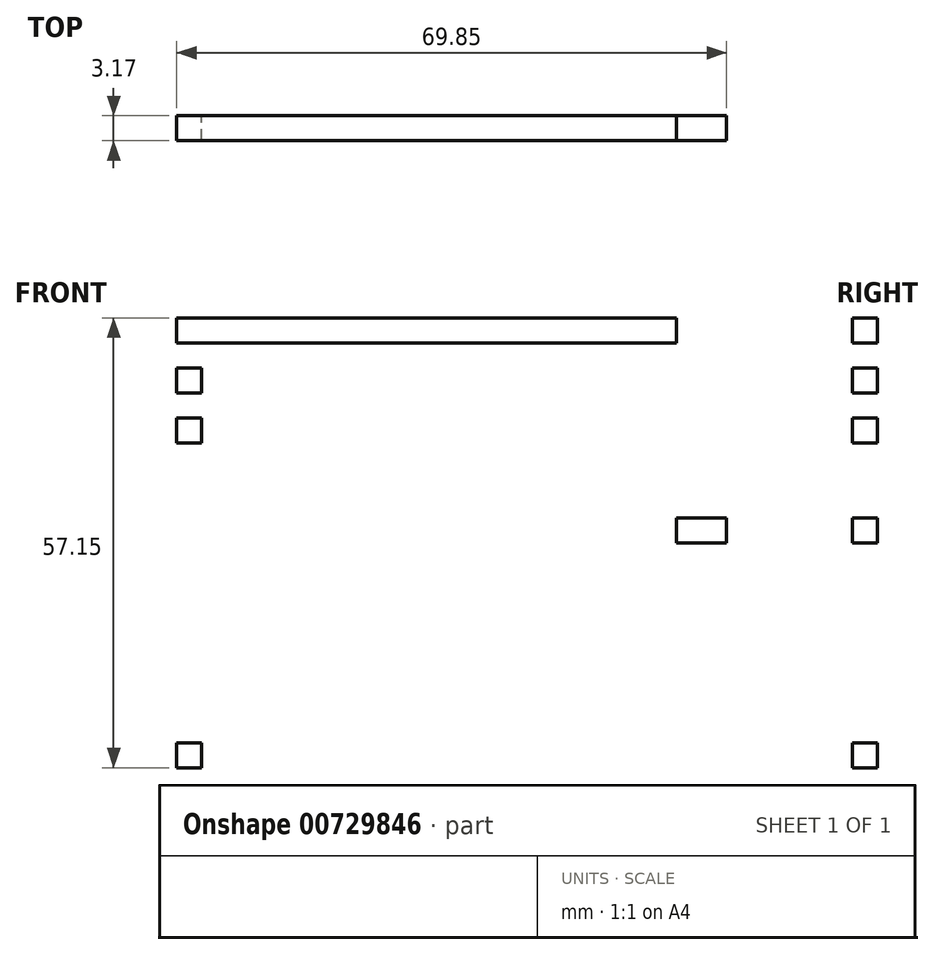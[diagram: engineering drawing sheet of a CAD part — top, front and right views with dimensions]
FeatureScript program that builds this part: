
annotation { "Feature Type Name" : "Feature", "Feature Type Description" : "" }
export const myFeature = defineFeature(function(context is Context, id is Id, definition is map)
    precondition{}
    {
        {
            var Q0;
            Q0=qCreatedBy(makeId("Front.planeOp"),FACE);
            var sketch = newSketch(context, id + "F0", { "sketchPlane" : qUnion([Q0])});
            skLineSegment(sketch, "E0.bottom", {"start": v(-59.86, 11.25) * mm, "end": v(13.17, 11.25) * mm});
            skLineSegment(sketch, "E0.top", {"start": v(-59.86, -39.55) * mm, "end": v(13.17, -39.55) * mm});
            skLineSegment(sketch, "E0.left", {"start": v(-59.86, 11.25) * mm, "end": v(-59.86, -39.55) * mm});
            skLineSegment(sketch, "E0.right", {"start": v(13.17, 11.25) * mm, "end": v(13.17, -39.55) * mm});
            skLineSegment(sketch, "E1.bottom", {"start": v(-53.5, -39.55) * mm, "end": v(10, -39.55) * mm});
            skLineSegment(sketch, "E1.top", {"start": v(-53.5, -42.73) * mm, "end": v(6.82, -42.73) * mm});
            skLineSegment(sketch, "E1.left", {"start": v(-53.5, -39.55) * mm, "end": v(-53.5, -42.73) * mm});
            skLineSegment(sketch, "E2.bottom", {"start": v(-56.68, 11.25) * mm, "end": v(6.82, 11.25) * mm});
            skLineSegment(sketch, "E2.top", {"start": v(-56.68, 14.42) * mm, "end": v(6.82, 14.42) * mm});
            skLineSegment(sketch, "E2.left", {"start": v(-56.68, 11.25) * mm, "end": v(-56.68, 14.42) * mm});
            skLineSegment(sketch, "E2.right", {"start": v(6.82, 11.25) * mm, "end": v(6.82, 14.42) * mm});
            skLineSegment(sketch, "E3.bottom", {"start": v(-56.68, 11.25) * mm, "end": v(-59.86, 11.25) * mm});
            skLineSegment(sketch, "E3.top", {"start": v(-56.68, -39.55) * mm, "end": v(-59.86, -39.55) * mm});
            skLineSegment(sketch, "E3.left", {"start": v(-56.68, 11.25) * mm, "end": v(-56.68, -39.55) * mm});
            skLineSegment(sketch, "E4.bottom", {"start": v(-53.5, -39.55) * mm, "end": v(-59.86, -39.55) * mm});
            skLineSegment(sketch, "E4.top", {"start": v(-53.5, 4.9) * mm, "end": v(-59.86, 4.9) * mm});
            skLineSegment(sketch, "E4.left", {"start": v(-53.5, -39.55) * mm, "end": v(-53.5, 4.9) * mm});
            skLineSegment(sketch, "E4.right", {"start": v(-59.86, -39.55) * mm, "end": v(-59.86, 4.9) * mm});
            skLineSegment(sketch, "E5.top", {"start": v(-56.68, -1.45) * mm, "end": v(-59.86, -1.45) * mm});
            skLineSegment(sketch, "E5.left", {"start": v(-56.68, -39.55) * mm, "end": v(-56.68, -1.45) * mm});
            skLineSegment(sketch, "E5.right", {"start": v(-59.86, -39.55) * mm, "end": v(-59.86, -1.45) * mm});
            skLineSegment(sketch, "E6.top", {"start": v(-56.68, -7.8) * mm, "end": v(-59.86, -7.8) * mm});
            skLineSegment(sketch, "E6.left", {"start": v(-56.68, -39.55) * mm, "end": v(-56.68, -7.8) * mm});
            skLineSegment(sketch, "E6.right", {"start": v(-59.86, -39.55) * mm, "end": v(-59.86, -7.8) * mm});
            skLineSegment(sketch, "E7.top", {"start": v(-53.5, -20.5) * mm, "end": v(-59.86, -20.5) * mm});
            skLineSegment(sketch, "E7.left", {"start": v(-53.5, -39.55) * mm, "end": v(-53.5, -20.5) * mm});
            skLineSegment(sketch, "E7.right", {"start": v(-59.86, -39.55) * mm, "end": v(-59.86, -20.5) * mm});
            skLineSegment(sketch, "E8.bottom", {"start": v(-59.86, -14.15) * mm, "end": v(-53.5, -14.15) * mm});
            skLineSegment(sketch, "E8.top", {"start": v(-59.86, -39.55) * mm, "end": v(-53.5, -39.55) * mm});
            skLineSegment(sketch, "E8.left", {"start": v(-59.86, -14.15) * mm, "end": v(-59.86, -39.55) * mm});
            skLineSegment(sketch, "E8.right", {"start": v(-53.5, -14.15) * mm, "end": v(-53.5, -39.55) * mm});
            skLineSegment(sketch, "E9.bottom", {"start": v(-59.86, -26.85) * mm, "end": v(-53.5, -26.85) * mm});
            skLineSegment(sketch, "E9.left", {"start": v(-59.86, -26.85) * mm, "end": v(-59.86, -39.55) * mm});
            skLineSegment(sketch, "E9.right", {"start": v(-53.5, -26.85) * mm, "end": v(-53.5, -39.55) * mm});
            skLineSegment(sketch, "E10.bottom", {"start": v(-59.86, -33.2) * mm, "end": v(-56.68, -33.2) * mm});
            skLineSegment(sketch, "E10.top", {"start": v(-59.86, -39.55) * mm, "end": v(-56.68, -39.55) * mm});
            skLineSegment(sketch, "E10.left", {"start": v(-59.86, -33.2) * mm, "end": v(-59.86, -39.55) * mm});
            skLineSegment(sketch, "E10.right", {"start": v(-56.68, -33.2) * mm, "end": v(-56.68, -39.55) * mm});
            skLineSegment(sketch, "E11.bottom", {"start": v(6.82, 11.25) * mm, "end": v(13.17, 11.25) * mm});
            skLineSegment(sketch, "E11.top", {"start": v(6.82, -33.2) * mm, "end": v(13.17, -33.2) * mm});
            skLineSegment(sketch, "E11.left", {"start": v(6.82, 11.25) * mm, "end": v(6.82, -33.2) * mm});
            skLineSegment(sketch, "E11.right", {"start": v(13.17, 11.25) * mm, "end": v(13.17, -33.2) * mm});
            skLineSegment(sketch, "E12.top", {"start": v(6.82, -26.85) * mm, "end": v(13.17, -26.85) * mm});
            skLineSegment(sketch, "E12.left", {"start": v(6.82, 11.25) * mm, "end": v(6.82, -26.85) * mm});
            skLineSegment(sketch, "E12.right", {"start": v(13.17, 11.25) * mm, "end": v(13.17, -26.85) * mm});
            skLineSegment(sketch, "E13.top", {"start": v(6.82, -39.55) * mm, "end": v(13.17, -39.55) * mm});
            skLineSegment(sketch, "E13.left", {"start": v(6.82, 11.25) * mm, "end": v(6.82, -39.55) * mm});
            skLineSegment(sketch, "E14.top", {"start": v(6.82, -14.15) * mm, "end": v(13.17, -14.15) * mm});
            skLineSegment(sketch, "E14.left", {"start": v(6.82, 11.25) * mm, "end": v(6.82, -14.15) * mm});
            skLineSegment(sketch, "E14.right", {"start": v(13.17, 11.25) * mm, "end": v(13.17, -14.15) * mm});
            skLineSegment(sketch, "E15.top", {"start": v(6.82, -20.5) * mm, "end": v(13.17, -20.5) * mm});
            skLineSegment(sketch, "E15.left", {"start": v(6.82, 11.25) * mm, "end": v(6.82, -20.5) * mm});
            skLineSegment(sketch, "E15.right", {"start": v(13.17, 11.25) * mm, "end": v(13.17, -20.5) * mm});
            skLineSegment(sketch, "E16.top", {"start": v(6.82, -7.8) * mm, "end": v(13.17, -7.8) * mm});
            skLineSegment(sketch, "E16.left", {"start": v(6.82, 11.25) * mm, "end": v(6.82, -7.8) * mm});
            skLineSegment(sketch, "E16.right", {"start": v(13.17, 11.25) * mm, "end": v(13.17, -7.8) * mm});
            skLineSegment(sketch, "E17.top", {"start": v(6.82, -1.45) * mm, "end": v(13.17, -1.45) * mm});
            skLineSegment(sketch, "E17.left", {"start": v(6.82, 11.25) * mm, "end": v(6.82, -1.45) * mm});
            skLineSegment(sketch, "E17.right", {"start": v(13.17, 11.25) * mm, "end": v(13.17, -1.45) * mm});
            skLineSegment(sketch, "E18.top", {"start": v(6.82, 4.9) * mm, "end": v(13.17, 4.9) * mm});
            skLineSegment(sketch, "E18.left", {"start": v(6.82, 11.25) * mm, "end": v(6.82, 4.9) * mm});
            skLineSegment(sketch, "E18.right", {"start": v(13.17, 11.25) * mm, "end": v(13.17, 4.9) * mm});
            skLineSegment(sketch, "E19", {"start": v(-59.86, -7.8) * mm, "end": v(-53.5, -7.8) * mm});
            skLineSegment(sketch, "E20", {"start": v(-53.5, -42.73) * mm, "end": v(-53.5, 11.25) * mm});
            skLineSegment(sketch, "E21", {"start": v(-59.86, -1.45) * mm, "end": v(-53.5, -1.45) * mm});
            skLineSegment(sketch, "E22", {"start": v(-59.86, -33.2) * mm, "end": v(-53.5, -33.2) * mm});
            skLineSegment(sketch, "E23.bottom", {"start": v(6.82, -39.55) * mm, "end": v(-53.5, -39.55) * mm});
            skLineSegment(sketch, "E23.top", {"start": v(6.82, -42.73) * mm, "end": v(-53.5, -42.73) * mm});
            skLineSegment(sketch, "E23.left", {"start": v(6.82, -39.55) * mm, "end": v(6.82, -42.73) * mm});
            skLineSegment(sketch, "E24", {"start": v(10, -39.55) * mm, "end": v(10, 11.25) * mm});
            skLineSegment(sketch, "E25.bottom", {"start": v(13.17, 11.25) * mm, "end": v(6.82, 11.25) * mm});
            skLineSegment(sketch, "E25.top", {"start": v(13.17, 8.07) * mm, "end": v(6.82, 8.07) * mm});
            skLineSegment(sketch, "E25.left", {"start": v(13.17, 11.25) * mm, "end": v(13.17, 8.07) * mm});
            skLineSegment(sketch, "E25.right", {"start": v(6.82, 11.25) * mm, "end": v(6.82, 8.07) * mm});
            skLineSegment(sketch, "E26.bottom", {"start": v(13.17, 4.9) * mm, "end": v(6.82, 4.9) * mm});
            skLineSegment(sketch, "E26.top", {"start": v(13.17, 1.72) * mm, "end": v(6.82, 1.72) * mm});
            skLineSegment(sketch, "E26.left", {"start": v(13.17, 4.9) * mm, "end": v(13.17, 1.72) * mm});
            skLineSegment(sketch, "E26.right", {"start": v(6.82, 4.9) * mm, "end": v(6.82, 1.72) * mm});
            skLineSegment(sketch, "E27.bottom", {"start": v(13.17, -1.45) * mm, "end": v(6.82, -1.45) * mm});
            skLineSegment(sketch, "E27.top", {"start": v(13.17, -4.63) * mm, "end": v(6.82, -4.63) * mm});
            skLineSegment(sketch, "E27.left", {"start": v(13.17, -1.45) * mm, "end": v(13.17, -4.63) * mm});
            skLineSegment(sketch, "E27.right", {"start": v(6.82, -1.45) * mm, "end": v(6.82, -4.63) * mm});
            skLineSegment(sketch, "E28.bottom", {"start": v(13.17, -7.8) * mm, "end": v(6.82, -7.8) * mm});
            skLineSegment(sketch, "E28.top", {"start": v(13.17, -10.98) * mm, "end": v(6.82, -10.98) * mm});
            skLineSegment(sketch, "E28.left", {"start": v(13.17, -7.8) * mm, "end": v(13.17, -10.98) * mm});
            skLineSegment(sketch, "E28.right", {"start": v(6.82, -7.8) * mm, "end": v(6.82, -10.98) * mm});
            skLineSegment(sketch, "E29.bottom", {"start": v(-59.86, 11.25) * mm, "end": v(-53.5, 11.25) * mm});
            skLineSegment(sketch, "E29.top", {"start": v(-59.86, 8.07) * mm, "end": v(-53.5, 8.07) * mm});
            skLineSegment(sketch, "E29.left", {"start": v(-59.86, 11.25) * mm, "end": v(-59.86, 8.07) * mm});
            skLineSegment(sketch, "E29.right", {"start": v(-53.5, 11.25) * mm, "end": v(-53.5, 8.07) * mm});
            skLineSegment(sketch, "E30.top", {"start": v(-53.5, 1.72) * mm, "end": v(-59.86, 1.72) * mm});
            skLineSegment(sketch, "E30.left", {"start": v(-53.5, 4.9) * mm, "end": v(-53.5, 1.72) * mm});
            skLineSegment(sketch, "E30.right", {"start": v(-59.86, 4.9) * mm, "end": v(-59.86, 1.72) * mm});
            skPoint(sketch, "E31.oppositeSnap0", {"position": v(-56.68, -36.38) * mm});
            skLineSegment(sketch, "E31.top", {"start": v(-59.86, -36.38) * mm, "end": v(-53.5, -36.38) * mm});
            skLineSegment(sketch, "E31.left", {"start": v(-59.86, -39.55) * mm, "end": v(-59.86, -36.38) * mm});
            skLineSegment(sketch, "E31.right", {"start": v(-53.5, -39.55) * mm, "end": v(-53.5, -36.38) * mm});
            skLineSegment(sketch, "E32.top", {"start": v(-59.86, -30.03) * mm, "end": v(-53.5, -30.03) * mm});
            skLineSegment(sketch, "E32.left", {"start": v(-59.86, -33.2) * mm, "end": v(-59.86, -30.03) * mm});
            skLineSegment(sketch, "E32.right", {"start": v(-53.5, -33.2) * mm, "end": v(-53.5, -30.03) * mm});
            skLineSegment(sketch, "E33.top", {"start": v(-59.86, -23.68) * mm, "end": v(-53.5, -23.68) * mm});
            skLineSegment(sketch, "E33.left", {"start": v(-59.86, -26.85) * mm, "end": v(-59.86, -23.68) * mm});
            skLineSegment(sketch, "E33.right", {"start": v(-53.5, -26.85) * mm, "end": v(-53.5, -23.68) * mm});
            skLineSegment(sketch, "E34.bottom", {"start": v(-59.86, -20.5) * mm, "end": v(-53.5, -20.5) * mm});
            skLineSegment(sketch, "E34.top", {"start": v(-59.86, -17.33) * mm, "end": v(-53.5, -17.33) * mm});
            skLineSegment(sketch, "E34.left", {"start": v(-59.86, -20.5) * mm, "end": v(-59.86, -17.33) * mm});
            skLineSegment(sketch, "E34.right", {"start": v(-53.5, -20.5) * mm, "end": v(-53.5, -17.33) * mm});
            skLineSegment(sketch, "E35.top", {"start": v(-59.86, -10.98) * mm, "end": v(-53.5, -10.98) * mm});
            skLineSegment(sketch, "E35.left", {"start": v(-59.86, -14.15) * mm, "end": v(-59.86, -10.98) * mm});
            skLineSegment(sketch, "E35.right", {"start": v(-53.5, -14.15) * mm, "end": v(-53.5, -10.98) * mm});
            skLineSegment(sketch, "E36.bottom", {"start": v(-53.5, -7.8) * mm, "end": v(-59.86, -7.8) * mm});
            skLineSegment(sketch, "E36.top", {"start": v(-53.5, -4.63) * mm, "end": v(-59.86, -4.63) * mm});
            skLineSegment(sketch, "E36.left", {"start": v(-53.5, -7.8) * mm, "end": v(-53.5, -4.63) * mm});
            skLineSegment(sketch, "E36.right", {"start": v(-59.86, -7.8) * mm, "end": v(-59.86, -4.63) * mm});
            skLineSegment(sketch, "E37.bottom", {"start": v(13.17, -39.55) * mm, "end": v(6.82, -39.55) * mm});
            skLineSegment(sketch, "E37.top", {"start": v(13.17, -36.38) * mm, "end": v(6.82, -36.38) * mm});
            skLineSegment(sketch, "E37.left", {"start": v(13.17, -39.55) * mm, "end": v(13.17, -36.38) * mm});
            skLineSegment(sketch, "E37.right", {"start": v(6.82, -39.55) * mm, "end": v(6.82, -36.38) * mm});
            skLineSegment(sketch, "E38.bottom", {"start": v(13.17, -33.2) * mm, "end": v(6.82, -33.2) * mm});
            skLineSegment(sketch, "E38.top", {"start": v(13.17, -30.03) * mm, "end": v(6.82, -30.03) * mm});
            skLineSegment(sketch, "E38.left", {"start": v(13.17, -33.2) * mm, "end": v(13.17, -30.03) * mm});
            skLineSegment(sketch, "E38.right", {"start": v(6.82, -33.2) * mm, "end": v(6.82, -30.03) * mm});
            skLineSegment(sketch, "E39.bottom", {"start": v(13.17, -26.85) * mm, "end": v(6.82, -26.85) * mm});
            skLineSegment(sketch, "E39.top", {"start": v(13.17, -23.68) * mm, "end": v(6.82, -23.68) * mm});
            skLineSegment(sketch, "E39.left", {"start": v(13.17, -26.85) * mm, "end": v(13.17, -23.68) * mm});
            skLineSegment(sketch, "E39.right", {"start": v(6.82, -26.85) * mm, "end": v(6.82, -23.68) * mm});
            skLineSegment(sketch, "E40.bottom", {"start": v(13.17, -20.5) * mm, "end": v(6.82, -20.5) * mm});
            skLineSegment(sketch, "E40.top", {"start": v(13.17, -17.33) * mm, "end": v(6.82, -17.33) * mm});
            skLineSegment(sketch, "E40.left", {"start": v(13.17, -20.5) * mm, "end": v(13.17, -17.33) * mm});
            skLineSegment(sketch, "E40.right", {"start": v(6.82, -20.5) * mm, "end": v(6.82, -17.33) * mm});
            skLineSegment(sketch, "E41.bottom", {"start": v(-53.5, -42.73) * mm, "end": v(-56.68, -42.73) * mm});
            skLineSegment(sketch, "E41.top", {"start": v(-53.5, -39.55) * mm, "end": v(-56.68, -39.55) * mm});
            skLineSegment(sketch, "E41.left", {"start": v(-53.5, -42.73) * mm, "end": v(-53.5, -39.55) * mm});
            skLineSegment(sketch, "E41.right", {"start": v(-56.68, -42.73) * mm, "end": v(-56.68, -39.55) * mm});
            skLineSegment(sketch, "E42.bottom", {"start": v(67.14, -44.56) * mm, "end": v(67.14, -44.56) * mm});
            skLineSegment(sketch, "E42.top", {"start": v(67.14, -48.1) * mm, "end": v(67.14, -48.1) * mm});
            skLineSegment(sketch, "E42.left", {"start": v(67.14, -44.56) * mm, "end": v(67.14, -48.1) * mm});
            skLineSegment(sketch, "E42.right", {"start": v(67.14, -44.56) * mm, "end": v(67.14, -48.1) * mm});
            skPoint(sketch, "E1.right.end.orphan", {"position": v(67.14, -42.73) * mm});
            skLineSegment(sketch, "E43.bottom", {"start": v(-23.34, 11.25) * mm, "end": v(-4.3, 11.25) * mm});
            skLineSegment(sketch, "E43.top", {"start": v(-23.34, -39.55) * mm, "end": v(-4.3, -39.55) * mm});
            skLineSegment(sketch, "E43.left", {"start": v(-23.34, 11.25) * mm, "end": v(-23.34, -39.55) * mm});
            skLineSegment(sketch, "E43.right", {"start": v(-4.3, 11.25) * mm, "end": v(-4.3, -39.55) * mm});
            skLineSegment(sketch, "E44.bottom", {"start": v(-23.34, 11.25) * mm, "end": v(-42.4, 11.25) * mm});
            skLineSegment(sketch, "E44.top", {"start": v(-23.34, -39.55) * mm, "end": v(-42.4, -39.55) * mm});
            skLineSegment(sketch, "E44.right", {"start": v(-42.4, 11.25) * mm, "end": v(-42.4, -39.55) * mm});
            skSolve(sketch);
        }
        {
            var Q0;
            Q0=makeQuery(id+"F0.imprint","IMPRINT",FACE,{"disambiguationData":[TD([[makeQuery(id+"F0.imprint","IMPRINT",EDGE,{"derivedFrom":sQuery(id+"F0.wireOp",EDGE,"E2.top")}),-1.0]])]});
            var Q1;
            {var subQ5=sQuery(id+"F0.wireOp",EDGE,"E29.right");Q1=makeQuery(id+"F0.imprint","IMPRINT",FACE,{"disambiguationData":[TD([[makeQuery(id+"F0.imprint","IMPRINT",EDGE,{"derivedFrom":subQ5}),-1.0]])]});}
            var Q2;
            {var subQ0=sQuery(id+"F0.wireOp",EDGE,"E29.top");var subQ1=sQuery(id+"F0.wireOp",EDGE,"E3.left");var subQ2=makeQuery(id+"F0.imprint","INTERSECT",VERTEX,{"derivedFrom":[subQ1,subQ0]});Q2=makeQuery(id+"F0.imprint","IMPRINT",FACE,{"disambiguationData":[TD([[makeQuery(id+"F0.imprint","IMPRINT",EDGE,{"disambiguationData":[TD([[subQ2,-1.0]])],"derivedFrom":subQ1}),1.0]])]});}
            var Q3;
            {var subQ5=sQuery(id+"F0.wireOp",EDGE,"E30.left");Q3=makeQuery(id+"F0.imprint","IMPRINT",FACE,{"disambiguationData":[TD([[makeQuery(id+"F0.imprint","IMPRINT",EDGE,{"derivedFrom":subQ5}),-1.0]])]});}
            var Q4;
            {var subQ1=sQuery(id+"F0.wireOp",EDGE,"E3.left");var subQ3=sQuery(id+"F0.wireOp",EDGE,"E30.top");var subQ4=makeQuery(id+"F0.imprint","INTERSECT",VERTEX,{"derivedFrom":[subQ1,subQ3]});Q4=makeQuery(id+"F0.imprint","IMPRINT",FACE,{"disambiguationData":[TD([[makeQuery(id+"F0.imprint","IMPRINT",EDGE,{"disambiguationData":[TD([[subQ4,-1.0]])],"derivedFrom":subQ1}),1.0]])]});}
            var Q5;
            Q5=makeQuery(id+"F0.imprint","IMPRINT",FACE,{"disambiguationData":[TD([[makeQuery(id+"F0.imprint","IMPRINT",EDGE,{"derivedFrom":sQuery(id+"F0.wireOp",EDGE,"E16.left")}),-1.0]])]});
            var Q6;
            {var subQ10=sQuery(id+"F0.wireOp",EDGE,"IFYuOt5v-Vo9e-aLds-Uov3-NytiRBSH38YG");Q6=makeQuery(id+"F0.imprint","IMPRINT",FACE,{"disambiguationData":[TD([[makeQuery(id+"F0.imprint","IMPRINT",EDGE,{"derivedFrom":subQ10}),-1.0]])]});}
            var Q7;
            {var subQ0=sQuery(id+"F0.wireOp",EDGE,"E18.left");Q7=makeQuery(id+"F0.imprint","IMPRINT",FACE,{"disambiguationData":[TD([[makeQuery(id+"F0.imprint","IMPRINT",EDGE,{"derivedFrom":subQ0}),1.0]])]});}
            var Q8;
            {var subQ0=sQuery(id+"F0.wireOp",EDGE,"E17.left");Q8=makeQuery(id+"F0.imprint","IMPRINT",FACE,{"disambiguationData":[TD([[makeQuery(id+"F0.imprint","IMPRINT",EDGE,{"derivedFrom":subQ0}),1.0]])]});}
            var Q9;
            {var subQ0=sQuery(id+"F0.wireOp",EDGE,"E16.left");Q9=makeQuery(id+"F0.imprint","IMPRINT",FACE,{"disambiguationData":[TD([[makeQuery(id+"F0.imprint","IMPRINT",EDGE,{"derivedFrom":subQ0}),1.0]])]});}
            var Q10;
            {var subQ0=sQuery(id+"F0.wireOp",EDGE,"E15.left");var subQ1=sQuery(id+"F0.wireOp",EDGE,"E14.top");var subQ2=makeQuery(id+"F0.imprint","INTERSECT",VERTEX,{"derivedFrom":[subQ1,subQ0]});Q10=makeQuery(id+"F0.imprint","IMPRINT",FACE,{"disambiguationData":[TD([[makeQuery(id+"F0.imprint","IMPRINT",EDGE,{"disambiguationData":[TD([[subQ2,-1.0]])],"derivedFrom":subQ1}),1.0]])]});}
            var Q11;
            {var subQ5=sQuery(id+"F0.wireOp",EDGE,"E40.right");Q11=makeQuery(id+"F0.imprint","IMPRINT",FACE,{"disambiguationData":[TD([[makeQuery(id+"F0.imprint","IMPRINT",EDGE,{"derivedFrom":subQ5}),-1.0]])]});}
            var Q12;
            {var subQ5=sQuery(id+"F0.wireOp",EDGE,"E39.right");Q12=makeQuery(id+"F0.imprint","IMPRINT",FACE,{"disambiguationData":[TD([[makeQuery(id+"F0.imprint","IMPRINT",EDGE,{"derivedFrom":subQ5}),-1.0]])]});}
            var Q13;
            {var subQ5=sQuery(id+"F0.wireOp",EDGE,"E38.right");Q13=makeQuery(id+"F0.imprint","IMPRINT",FACE,{"disambiguationData":[TD([[makeQuery(id+"F0.imprint","IMPRINT",EDGE,{"derivedFrom":subQ5}),-1.0]])]});}
            var Q14;
            {var subQ5=sQuery(id+"F0.wireOp",EDGE,"E37.right");Q14=makeQuery(id+"F0.imprint","IMPRINT",FACE,{"disambiguationData":[TD([[makeQuery(id+"F0.imprint","IMPRINT",EDGE,{"derivedFrom":subQ5}),-1.0]])]});}
            var Q15;
            Q15=makeQuery(id+"F0.imprint","IMPRINT",FACE,{"disambiguationData":[TD([[makeQuery(id+"F0.imprint","IMPRINT",EDGE,{"derivedFrom":sQuery(id+"F0.wireOp",EDGE,"E23.top")}),-1.0]])]});
            var Q16;
            {var subQ1=sQuery(id+"F0.wireOp",EDGE,"E5.left");var subQ3=sQuery(id+"F0.wireOp",EDGE,"E36.top");var subQ4=makeQuery(id+"F0.imprint","INTERSECT",VERTEX,{"derivedFrom":[subQ1,subQ3]});Q16=makeQuery(id+"F0.imprint","IMPRINT",FACE,{"disambiguationData":[TD([[makeQuery(id+"F0.imprint","IMPRINT",EDGE,{"disambiguationData":[TD([[subQ4,-1.0]])],"derivedFrom":subQ1}),-1.0]])]});}
            var Q17;
            {var subQ5=sQuery(id+"F0.wireOp",EDGE,"E36.left");Q17=makeQuery(id+"F0.imprint","IMPRINT",FACE,{"disambiguationData":[TD([[makeQuery(id+"F0.imprint","IMPRINT",EDGE,{"derivedFrom":subQ5}),1.0]])]});}
            var Q18;
            Q18=makeQuery(id+"F0.imprint","IMPRINT",FACE,{"disambiguationData":[TD([[makeQuery(id+"F0.imprint","IMPRINT",EDGE,{"derivedFrom":sQuery(id+"F0.wireOp",EDGE,"E41.bottom")}),-1.0]])]});
            var Q19;
            {var subQ4=sQuery(id+"F0.wireOp",EDGE,"E31.right");Q19=makeQuery(id+"F0.imprint","IMPRINT",FACE,{"disambiguationData":[TD([[makeQuery(id+"F0.imprint","IMPRINT",EDGE,{"derivedFrom":subQ4}),1.0]])]});}
            var Q20;
            {var subQ0=sQuery(id+"F0.wireOp",EDGE,"E32.top");var subQ1=sQuery(id+"F0.wireOp",EDGE,"E6.left");var subQ2=makeQuery(id+"F0.imprint","INTERSECT",VERTEX,{"derivedFrom":[subQ1,subQ0]});Q20=makeQuery(id+"F0.imprint","IMPRINT",FACE,{"disambiguationData":[TD([[makeQuery(id+"F0.imprint","IMPRINT",EDGE,{"disambiguationData":[TD([[subQ2,-1.0]])],"derivedFrom":subQ1}),-1.0]])]});}
            var Q21;
            {var subQ5=sQuery(id+"F0.wireOp",EDGE,"E32.right");Q21=makeQuery(id+"F0.imprint","IMPRINT",FACE,{"disambiguationData":[TD([[makeQuery(id+"F0.imprint","IMPRINT",EDGE,{"derivedFrom":subQ5}),1.0]])]});}
            var Q22;
            {var subQ0=sQuery(id+"F0.wireOp",EDGE,"E34.top");var subQ1=sQuery(id+"F0.wireOp",EDGE,"E6.left");var subQ2=makeQuery(id+"F0.imprint","INTERSECT",VERTEX,{"derivedFrom":[subQ1,subQ0]});Q22=makeQuery(id+"F0.imprint","IMPRINT",FACE,{"disambiguationData":[TD([[makeQuery(id+"F0.imprint","IMPRINT",EDGE,{"disambiguationData":[TD([[subQ2,-1.0]])],"derivedFrom":subQ1}),-1.0]])]});}
            var Q23;
            {var subQ5=sQuery(id+"F0.wireOp",EDGE,"E34.right");Q23=makeQuery(id+"F0.imprint","IMPRINT",FACE,{"disambiguationData":[TD([[makeQuery(id+"F0.imprint","IMPRINT",EDGE,{"derivedFrom":subQ5}),1.0]])]});}
            var Q24;
            {var subQ0=sQuery(id+"F0.wireOp",EDGE,"E33.top");var subQ1=sQuery(id+"F0.wireOp",EDGE,"E6.left");var subQ2=makeQuery(id+"F0.imprint","INTERSECT",VERTEX,{"derivedFrom":[subQ1,subQ0]});Q24=makeQuery(id+"F0.imprint","IMPRINT",FACE,{"disambiguationData":[TD([[makeQuery(id+"F0.imprint","IMPRINT",EDGE,{"disambiguationData":[TD([[subQ2,-1.0]])],"derivedFrom":subQ1}),-1.0]])]});}
            var Q25;
            {var subQ5=sQuery(id+"F0.wireOp",EDGE,"E33.right");Q25=makeQuery(id+"F0.imprint","IMPRINT",FACE,{"disambiguationData":[TD([[makeQuery(id+"F0.imprint","IMPRINT",EDGE,{"derivedFrom":subQ5}),1.0]])]});}
            var Q26;
            {var subQ1=sQuery(id+"F0.wireOp",EDGE,"E10.right");var subQ3=sQuery(id+"F0.wireOp",EDGE,"E31.top");var subQ4=makeQuery(id+"F0.imprint","INTERSECT",VERTEX,{"derivedFrom":[subQ1,subQ3]});Q26=makeQuery(id+"F0.imprint","IMPRINT",FACE,{"disambiguationData":[TD([[makeQuery(id+"F0.imprint","IMPRINT",EDGE,{"disambiguationData":[TD([[subQ4,1.0]])],"derivedFrom":subQ1}),1.0]])]});}
            var Q27;
            {var subQ1=sQuery(id+"F0.wireOp",EDGE,"E6.left");var subQ3=sQuery(id+"F0.wireOp",EDGE,"E35.top");var subQ4=makeQuery(id+"F0.imprint","INTERSECT",VERTEX,{"derivedFrom":[subQ1,subQ3]});Q27=makeQuery(id+"F0.imprint","IMPRINT",FACE,{"disambiguationData":[TD([[makeQuery(id+"F0.imprint","IMPRINT",EDGE,{"disambiguationData":[TD([[subQ4,-1.0]])],"derivedFrom":subQ1}),-1.0]])]});}
            var Q28;
            {var subQ5=sQuery(id+"F0.wireOp",EDGE,"E35.right");Q28=makeQuery(id+"F0.imprint","IMPRINT",FACE,{"disambiguationData":[TD([[makeQuery(id+"F0.imprint","IMPRINT",EDGE,{"derivedFrom":subQ5}),1.0]])]});}
            var Q29;
            {var subQ5=sQuery(id+"F0.wireOp",EDGE,"E0.left");Q29=makeQuery(id+"F0.imprint","IMPRINT",FACE,{"disambiguationData":[TD([[makeQuery(id+"F0.imprint","IMPRINT",EDGE,{"derivedFrom":subQ5}),1.0]])]});}
            var Q30;
            {var subQ5=sQuery(id+"F0.wireOp",EDGE,"E4.right");Q30=makeQuery(id+"F0.imprint","IMPRINT",FACE,{"disambiguationData":[TD([[makeQuery(id+"F0.imprint","IMPRINT",EDGE,{"derivedFrom":subQ5}),-1.0]])]});}
            var Q31;
            {var subQ5=sQuery(id+"F0.wireOp",EDGE,"E36.right");Q31=makeQuery(id+"F0.imprint","IMPRINT",FACE,{"disambiguationData":[TD([[makeQuery(id+"F0.imprint","IMPRINT",EDGE,{"derivedFrom":subQ5}),-1.0]])]});}
            var Q32;
            {var subQ5=sQuery(id+"F0.wireOp",EDGE,"E35.left");Q32=makeQuery(id+"F0.imprint","IMPRINT",FACE,{"disambiguationData":[TD([[makeQuery(id+"F0.imprint","IMPRINT",EDGE,{"derivedFrom":subQ5}),-1.0]])]});}
            var Q33;
            {var subQ5=sQuery(id+"F0.wireOp",EDGE,"E34.left");Q33=makeQuery(id+"F0.imprint","IMPRINT",FACE,{"disambiguationData":[TD([[makeQuery(id+"F0.imprint","IMPRINT",EDGE,{"derivedFrom":subQ5}),-1.0]])]});}
            var Q34;
            {var subQ5=sQuery(id+"F0.wireOp",EDGE,"E33.left");Q34=makeQuery(id+"F0.imprint","IMPRINT",FACE,{"disambiguationData":[TD([[makeQuery(id+"F0.imprint","IMPRINT",EDGE,{"derivedFrom":subQ5}),-1.0]])]});}
            var Q35;
            {var subQ5=sQuery(id+"F0.wireOp",EDGE,"E32.left");Q35=makeQuery(id+"F0.imprint","IMPRINT",FACE,{"disambiguationData":[TD([[makeQuery(id+"F0.imprint","IMPRINT",EDGE,{"derivedFrom":subQ5}),-1.0]])]});}
            var Q36;
            {var subQ0=sQuery(id+"F0.wireOp",EDGE,"E8.top");Q36=makeQuery(id+"F0.imprint","IMPRINT",FACE,{"disambiguationData":[TD([[makeQuery(id+"F0.imprint","IMPRINT",EDGE,{"derivedFrom":subQ0}),1.0]])]});}
            var Q37;
            {var subQ0=sQuery(id+"F0.wireOp",EDGE,"E29.right");Q37=makeQuery(id+"F0.imprint","IMPRINT",FACE,{"disambiguationData":[TD([[makeQuery(id+"F0.imprint","IMPRINT",EDGE,{"derivedFrom":subQ0}),1.0]])]});}
            extrude(context, id + "F1", {"entities" : qUnion([Q0, Q1, Q2, Q3, Q4, Q5, Q6, Q7, Q8, Q9, Q10, Q11, Q12, Q13, Q14, Q15, Q16, Q17, Q18, Q19, Q20, Q21, Q22, Q23, Q24, Q25, Q26, Q27, Q28, Q29, Q30, Q31, Q32, Q33, Q34, Q35, Q36, Q37]), "depth" : 3.17 * mm, "offsetDistance" : 25.4 * mm});
        }
    });
